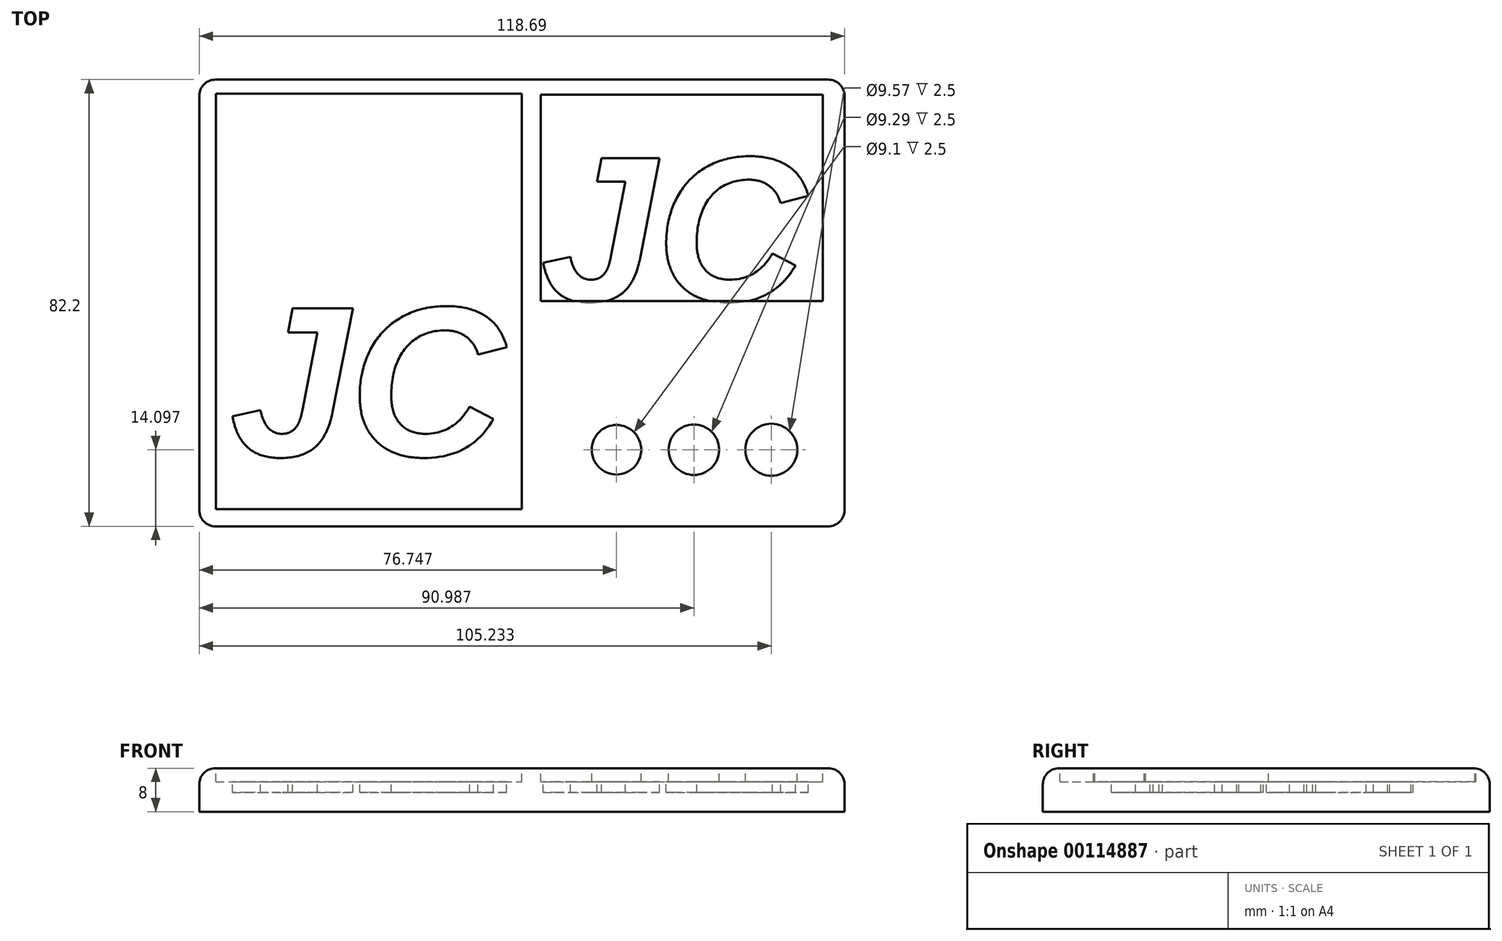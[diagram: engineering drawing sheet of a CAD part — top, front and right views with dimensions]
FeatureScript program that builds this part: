
annotation { "Feature Type Name" : "Feature", "Feature Type Description" : "" }
export const myFeature = defineFeature(function(context is Context, id is Id, definition is map)
    precondition{}
    {
        {
            var Q0;
            Q0=qCreatedBy(makeId("Top.planeOp"),FACE);
            var sketch = newSketch(context, id + "F0", { "sketchPlane" : qUnion([Q0])});
            skLineSegment(sketch, "E0.bottom", {"start": v(-62.8, 52.3) * mm, "end": v(55.88, 52.3) * mm});
            skLineSegment(sketch, "E0.top", {"start": v(-62.8, -29.9) * mm, "end": v(55.88, -29.9) * mm});
            skLineSegment(sketch, "E0.left", {"start": v(-62.8, 52.3) * mm, "end": v(-62.8, -29.9) * mm});
            skLineSegment(sketch, "E0.right", {"start": v(55.88, 52.3) * mm, "end": v(55.88, -29.9) * mm});
            skSolve(sketch);
        }
        {
            var Q0;
            Q0 = qSketchRegion(id + "F0", true);
            extrude(context, id + "F1", {"entities" : qUnion([Q0]), "depth" : 8 * mm});
        }
        {
            var Q0;
            Q0=makeQuery(id+"F1.opExtrude","CAP_FACE",FACE,{"disambiguationData":[OSD([sQuery(id+"F0.wireOp",EDGE,"E0.bottom"),sQuery(id+"F0.wireOp",EDGE,"E0.top"),sQuery(id+"F0.wireOp",EDGE,"E0.left"),sQuery(id+"F0.wireOp",EDGE,"E0.right")])],"isStart":false});
            var sketch = newSketch(context, id + "F2", { "sketchPlane" : qUnion([Q0])});
            skLineSegment(sketch, "E1.bottom", {"start": v(-59.72, -26.74) * mm, "end": v(-3.5, -26.74) * mm});
            skLineSegment(sketch, "E1.top", {"start": v(-59.72, 49.74) * mm, "end": v(-3.5, 49.74) * mm});
            skLineSegment(sketch, "E1.left", {"start": v(-59.72, -26.74) * mm, "end": v(-59.72, 49.74) * mm});
            skLineSegment(sketch, "E1.right", {"start": v(-3.5, -26.74) * mm, "end": v(-3.5, 49.74) * mm});
            skSolve(sketch);
        }
        {
            var Q0;
            Q0 = qSketchRegion(id + "F2", true);
            extrude(context, id + "F3", {"entities" : qUnion([Q0]), "operationType" : NewBodyOperationType.REMOVE, "oppositeDirection" : true, "depth" : 2.5 * mm});
        }
        {
            var Q0;
            Q0=makeQuery(id+"F1.opExtrude","CAP_FACE",FACE,{"disambiguationData":[OSD([sQuery(id+"F0.wireOp",EDGE,"E0.bottom"),sQuery(id+"F0.wireOp",EDGE,"E0.top"),sQuery(id+"F0.wireOp",EDGE,"E0.left"),sQuery(id+"F0.wireOp",EDGE,"E0.right")])],"isStart":false});
            var sketch = newSketch(context, id + "F4", { "sketchPlane" : qUnion([Q0])});
            skLineSegment(sketch, "E2.bottom", {"start": v(0, 49.54) * mm, "end": v(51.88, 49.54) * mm});
            skLineSegment(sketch, "E2.top", {"start": v(0, 11.56) * mm, "end": v(51.88, 11.56) * mm});
            skLineSegment(sketch, "E2.left", {"start": v(0, 49.54) * mm, "end": v(0, 11.56) * mm});
            skLineSegment(sketch, "E2.right", {"start": v(51.88, 49.54) * mm, "end": v(51.88, 11.56) * mm});
            skSolve(sketch);
        }
        {
            var Q0;
            Q0 = qSketchRegion(id + "F4", true);
            extrude(context, id + "F5", {"entities" : qUnion([Q0]), "operationType" : NewBodyOperationType.REMOVE, "oppositeDirection" : true, "depth" : 2.5 * mm});
        }
        {
            var Q0;
            Q0=makeQuery(id+"F1.opExtrude","CAP_FACE",FACE,{"disambiguationData":[OSD([sQuery(id+"F0.wireOp",EDGE,"E0.bottom"),sQuery(id+"F0.wireOp",EDGE,"E0.top"),sQuery(id+"F0.wireOp",EDGE,"E0.left"),sQuery(id+"F0.wireOp",EDGE,"E0.right")])],"isStart":false});
            var sketch = newSketch(context, id + "F6", { "sketchPlane" : qUnion([Q0])});
            skCircle(sketch, "E3", {"center": v(13.94, -15.8) * mm, "radius": 4.55 * mm});
            skCircle(sketch, "E4", {"center": v(28.18, -15.8) * mm, "radius": 4.64 * mm});
            skCircle(sketch, "E5", {"center": v(42.42, -15.8) * mm, "radius": 4.78 * mm});
            skSolve(sketch);
        }
        {
            var Q0;
            Q0 = qSketchRegion(id + "F6", true);
            extrude(context, id + "F7", {"entities" : qUnion([Q0]), "operationType" : NewBodyOperationType.REMOVE, "oppositeDirection" : true, "depth" : 2.5 * mm});
        }
        {
            var Q0;
            Q0=makeQuery(id+"F1.opExtrude","CAP_EDGE",EDGE,{"disambiguationData":[OSD([sQuery(id+"F0.wireOp",EDGE,"E0.right")])],"isStart":false});
            var Q1;
            Q1=makeQuery(id+"F1.opExtrude","CAP_EDGE",EDGE,{"disambiguationData":[OSD([sQuery(id+"F0.wireOp",EDGE,"E0.bottom")])],"isStart":false});
            var Q2;
            Q2=makeQuery(id+"F1.opExtrude","CAP_EDGE",EDGE,{"disambiguationData":[OSD([sQuery(id+"F0.wireOp",EDGE,"E0.left")])],"isStart":false});
            var Q3;
            Q3=makeQuery(id+"F1.opExtrude","CAP_EDGE",EDGE,{"disambiguationData":[OSD([sQuery(id+"F0.wireOp",EDGE,"E0.top")])],"isStart":false});
            var Q4;
            Q4=makeQuery(id+"F1.opExtrude","SWEPT_EDGE",EDGE,{"disambiguationData":[OSD([sQuery(id+"F0.wireOp",EDGE,"E0.top"),sQuery(id+"F0.wireOp",EDGE,"E0.right")])]});
            var Q5;
            Q5=makeQuery(id+"F1.opExtrude","SWEPT_EDGE",EDGE,{"disambiguationData":[OSD([sQuery(id+"F0.wireOp",EDGE,"E0.bottom"),sQuery(id+"F0.wireOp",EDGE,"E0.right")])]});
            var Q6;
            Q6=makeQuery(id+"F1.opExtrude","SWEPT_EDGE",EDGE,{"disambiguationData":[OSD([sQuery(id+"F0.wireOp",EDGE,"E0.top"),sQuery(id+"F0.wireOp",EDGE,"E0.left")])]});
            var Q7;
            Q7=makeQuery(id+"F1.opExtrude","SWEPT_EDGE",EDGE,{"disambiguationData":[OSD([sQuery(id+"F0.wireOp",EDGE,"E0.bottom"),sQuery(id+"F0.wireOp",EDGE,"E0.left")])]});
            fillet(context, id + "F8", {"entities" : qUnion([Q0, Q1, Q2, Q3, Q4, Q5, Q6, Q7]), "radius" : 3 * mm, "tangentPropagation" : true, "allowEdgeOverflow" : false});
        }
        {
            var Q0;
            Q0=makeQuery(id+"F3.boolean.opBoolean","COPY",FACE,{"derivedFrom":makeQuery(id+"F3.opExtrude","CAP_FACE",FACE,{"disambiguationData":[OSD([sQuery(id+"F2.wireOp",EDGE,"E1.bottom"),sQuery(id+"F2.wireOp",EDGE,"E1.top"),sQuery(id+"F2.wireOp",EDGE,"E1.left"),sQuery(id+"F2.wireOp",EDGE,"E1.right")])],"isStart":false})});
            var sketch = newSketch(context, id + "F9", { "sketchPlane" : qUnion([Q0])});
            skText(sketch, "E6", { "text": "JC", "fontName": "Arimo-BoldItalic.ttf"});
            const initialGuessF9  = {"E6": [-0.05718, -0.01694, 1, 0, 0.02843]};
            skSetInitialGuess(sketch, initialGuessF9);
            skSolve(sketch);
        }
        {
            var Q0;
            Q0 = qSketchRegion(id + "F9", true);
            extrude(context, id + "F10", {"entities" : qUnion([Q0]), "operationType" : NewBodyOperationType.REMOVE, "oppositeDirection" : true, "depth" : 2 * mm});
        }
        {
            var Q0;
            Q0=makeQuery(id+"F5.boolean.opBoolean","COPY",FACE,{"derivedFrom":makeQuery(id+"F5.opExtrude","CAP_FACE",FACE,{"disambiguationData":[OSD([sQuery(id+"F4.wireOp",EDGE,"E2.bottom"),sQuery(id+"F4.wireOp",EDGE,"E2.top"),sQuery(id+"F4.wireOp",EDGE,"E2.left"),sQuery(id+"F4.wireOp",EDGE,"E2.right")])],"isStart":false})});
            var sketch = newSketch(context, id + "F11", { "sketchPlane" : qUnion([Q0])});
            skText(sketch, "E7", { "text": "JC", "fontName": "Arimo-BoldItalic.ttf"});
            const initialGuessF11  = {"E7": [0, 0.01156, 1, 0, 0.02748]};
            skSetInitialGuess(sketch, initialGuessF11);
            skSolve(sketch);
        }
        {
            var Q0;
            Q0 = qSketchRegion(id + "F11", true);
            extrude(context, id + "F12", {"entities" : qUnion([Q0]), "operationType" : NewBodyOperationType.REMOVE, "oppositeDirection" : true, "depth" : 2 * mm});
        }
    });
